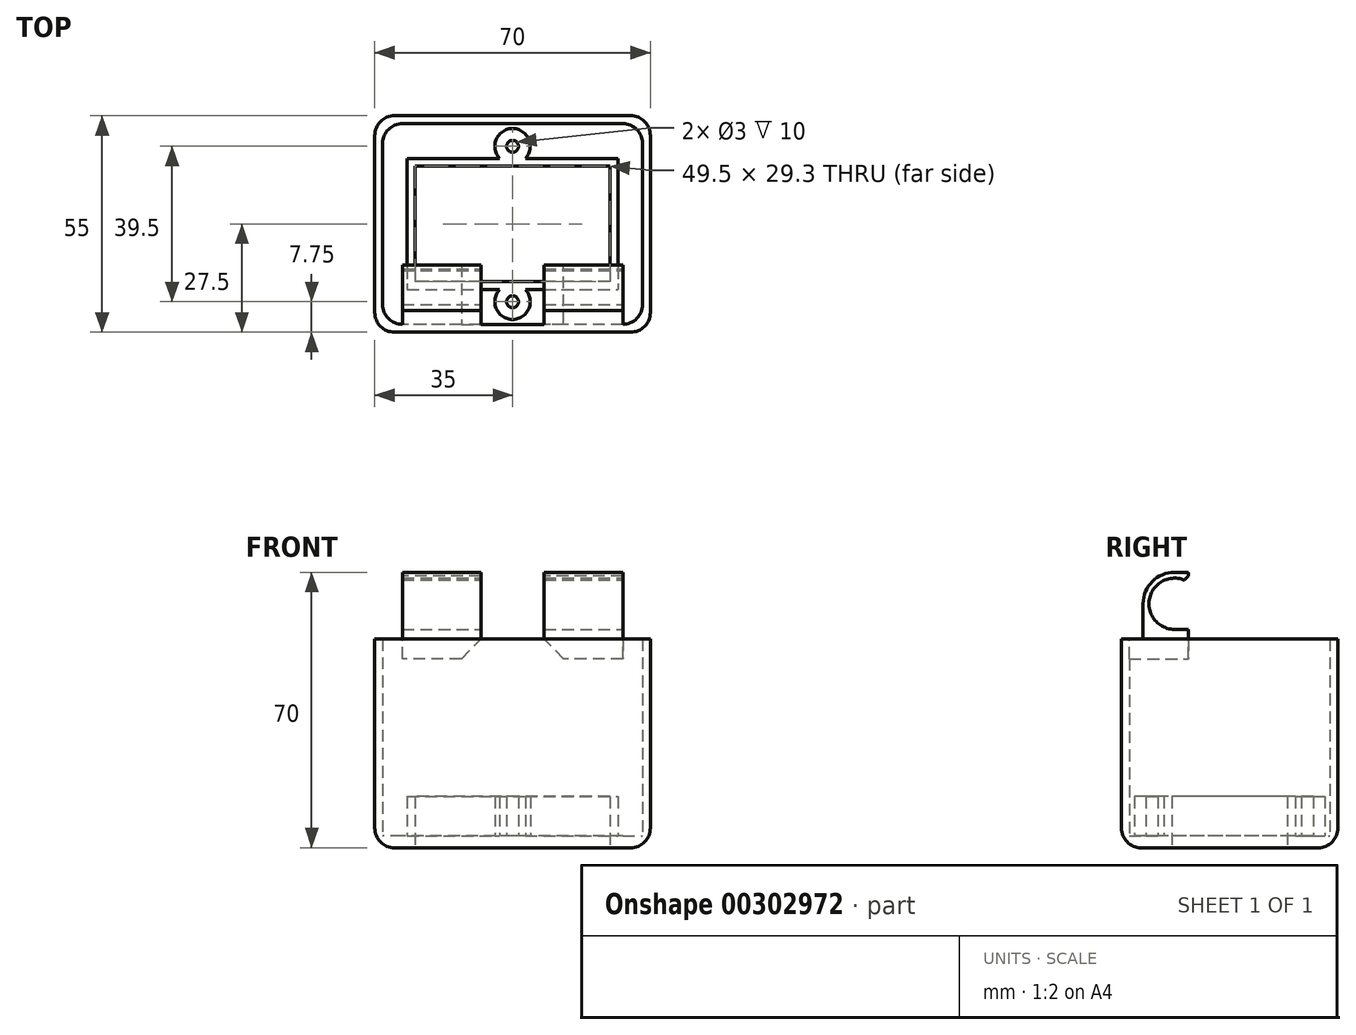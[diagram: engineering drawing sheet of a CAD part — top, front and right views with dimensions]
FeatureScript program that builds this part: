
annotation { "Feature Type Name" : "Feature", "Feature Type Description" : "" }
export const myFeature = defineFeature(function(context is Context, id is Id, definition is map)
    precondition{}
    {
        {
            var Q0;
            Q0=qCreatedBy(makeId("Top.planeOp"),FACE);
            var sketch = newSketch(context, id + "F0", { "sketchPlane" : qUnion([Q0])});
            skLineSegment(sketch, "E0.bottom", {"start": v(35, 27.5) * mm, "end": v(-35, 27.5) * mm});
            skLineSegment(sketch, "E0.top", {"start": v(35, -27.5) * mm, "end": v(-35, -27.5) * mm});
            skLineSegment(sketch, "E0.left", {"start": v(35, 27.5) * mm, "end": v(35, -27.5) * mm});
            skLineSegment(sketch, "E0.right", {"start": v(-35, 27.5) * mm, "end": v(-35, -27.5) * mm});
            skPoint(sketch, "E0.middle", {"position": v(0, 0) * mm});
            skLineSegment(sketch, "E1.bottom", {"start": v(24.75, 14.65) * mm, "end": v(-24.75, 14.65) * mm});
            skLineSegment(sketch, "E1.top", {"start": v(24.75, -14.65) * mm, "end": v(-24.75, -14.65) * mm});
            skLineSegment(sketch, "E1.left", {"start": v(24.75, 14.65) * mm, "end": v(24.75, -14.65) * mm});
            skLineSegment(sketch, "E1.right", {"start": v(-24.75, 14.65) * mm, "end": v(-24.75, -14.65) * mm});
            skSolve(sketch);
        }
        {
            var Q0;
            Q0=makeQuery(id+"F0.imprint","IMPRINT",FACE,{"disambiguationData":[TD([[makeQuery(id+"F0.imprint","IMPRINT",EDGE,{"derivedFrom":sQuery(id+"F0.wireOp",EDGE,"E0.bottom")}),1.0]])]});
            extrude(context, id + "F1", {"entities" : qUnion([Q0]), "depth" : 3 * mm, "offsetDistance" : 25 * mm});
        }
        {
            var Q0;
            Q0=makeQuery(id+"F1.opExtrude","CAP_FACE",FACE,{"disambiguationData":[OSD([sQuery(id+"F0.wireOp",EDGE,"E0.bottom"),sQuery(id+"F0.wireOp",EDGE,"E0.top"),sQuery(id+"F0.wireOp",EDGE,"E0.left"),sQuery(id+"F0.wireOp",EDGE,"E0.right"),sQuery(id+"F0.wireOp",EDGE,"E1.bottom"),sQuery(id+"F0.wireOp",EDGE,"E1.top"),sQuery(id+"F0.wireOp",EDGE,"E1.left"),sQuery(id+"F0.wireOp",EDGE,"E1.right")])],"isStart":false});
            var sketch = newSketch(context, id + "F2", { "sketchPlane" : qUnion([Q0])});
            skLineSegment(sketch, "E2.bottom", {"start": v(33, 25.5) * mm, "end": v(-33, 25.5) * mm});
            skLineSegment(sketch, "E2.top", {"start": v(33, -25.5) * mm, "end": v(-33, -25.5) * mm});
            skLineSegment(sketch, "E2.left", {"start": v(33, 25.5) * mm, "end": v(33, -25.5) * mm});
            skLineSegment(sketch, "E2.right", {"start": v(-33, 25.5) * mm, "end": v(-33, -25.5) * mm});
            skPoint(sketch, "E2.middle", {"position": v(0, 0) * mm});
            skLineSegment(sketch, "E3.bottom", {"start": v(-26.75, 16.65) * mm, "end": v(-3.26, 16.65) * mm});
            skLineSegment(sketch, "E3.top", {"start": v(-26.75, -16.65) * mm, "end": v(-3.26, -16.65) * mm});
            skLineSegment(sketch, "E3.left", {"start": v(-26.75, 16.65) * mm, "end": v(-26.75, -16.65) * mm});
            skLineSegment(sketch, "E3.right", {"start": v(26.75, 16.65) * mm, "end": v(26.75, -16.65) * mm});
            skLineSegment(sketch, "E4", {"start": v(0, 0) * mm, "end": v(0, 19.75) * mm, "construction": true});
            skLineSegment(sketch, "E5", {"start": v(0, 0) * mm, "end": v(0, -19.75) * mm, "construction": true});
            skPoint(sketch, "E5.endSnap0", {"position": v(0, -16.65) * mm});
            skCircle(sketch, "E6", {"center": v(0, 19.75) * mm, "radius": 1.5 * mm});
            skCircle(sketch, "E7", {"center": v(0, -19.75) * mm, "radius": 1.5 * mm});
            skArc(sketch, "E8", {"start": v(3.26, 16.65) * mm, "mid": v(0, 24.25) * mm, "end": v(-3.26, 16.65) * mm});
            skArc(sketch, "E9", {"start": v(-3.26, -16.65) * mm, "mid": v(0, -24.25) * mm, "end": v(3.26, -16.65) * mm});
            skLineSegment(sketch, "E10.trimOffspring", {"start": v(3.26, 16.65) * mm, "end": v(26.75, 16.65) * mm});
            skLineSegment(sketch, "E11.trimOffspring", {"start": v(3.26, -16.65) * mm, "end": v(26.75, -16.65) * mm});
            skSolve(sketch);
        }
        {
            var Q0;
            Q0=makeQuery(id+"F2.imprint","IMPRINT",FACE,{"disambiguationData":[TD([[makeQuery(id+"F2.imprint","IMPRINT",EDGE,{"derivedFrom":sQuery(id+"F2.wireOp",EDGE,"E3.bottom")}),-1.0]])]});
            extrude(context, id + "F3", {"entities" : qUnion([Q0]), "operationType" : NewBodyOperationType.ADD, "depth" : 10 * mm, "offsetDistance" : 25 * mm});
        }
        {
            var Q0;
            Q0=makeQuery(id+"F2.imprint","IMPRINT",FACE,{"disambiguationData":[TD([[makeQuery(id+"F2.imprint","IMPRINT",EDGE,{"derivedFrom":sQuery(id+"F2.wireOp",EDGE,"E2.bottom")}),-1.0]])]});
            extrude(context, id + "F4", {"entities" : qUnion([Q0]), "operationType" : NewBodyOperationType.ADD, "depth" : 50 * mm, "offsetDistance" : 25 * mm});
        }
        {
            var Q0;
            Q0=makeQuery(id+"F4.opExtrude","SWEPT_EDGE",EDGE,{"disambiguationData":[OSD([sQuery(id+"F2.wireOp",EDGE,"E2.bottom"),sQuery(id+"F2.wireOp",EDGE,"E2.right")])]});
            var Q1;
            Q1=makeQuery(id+"F4.opExtrude","SWEPT_EDGE",EDGE,{"disambiguationData":[OSD([sQuery(id+"F2.wireOp",EDGE,"E2.bottom"),sQuery(id+"F2.wireOp",EDGE,"E2.left")])]});
            var Q2;
            Q2=makeQuery(id+"F4.opExtrude","SWEPT_EDGE",EDGE,{"disambiguationData":[OSD([sQuery(id+"F2.wireOp",EDGE,"E2.top"),sQuery(id+"F2.wireOp",EDGE,"E2.right")])]});
            var Q3;
            Q3=makeQuery(id+"F4.opExtrude","SWEPT_EDGE",EDGE,{"disambiguationData":[OSD([sQuery(id+"F2.wireOp",EDGE,"E2.top"),sQuery(id+"F2.wireOp",EDGE,"E2.left")])]});
            var Q4;
            Q4=makeQuery(id+"F4.opExtrude","CAP_EDGE",EDGE,{"disambiguationData":[OSD([sQuery(id+"F2.wireOp",EDGE,"E2.bottom")])],"isStart":true});
            var Q5;
            Q5=makeQuery(id+"F4.opExtrude","CAP_EDGE",EDGE,{"disambiguationData":[OSD([sQuery(id+"F2.wireOp",EDGE,"E2.right")])],"isStart":true});
            var Q6;
            Q6=makeQuery(id+"F4.opExtrude","CAP_EDGE",EDGE,{"disambiguationData":[OSD([sQuery(id+"F2.wireOp",EDGE,"E2.left")])],"isStart":true});
            var Q7;
            Q7=makeQuery(id+"F4.opExtrude","CAP_EDGE",EDGE,{"disambiguationData":[OSD([sQuery(id+"F2.wireOp",EDGE,"E2.top")])],"isStart":true});
            var Q8;
            Q8=makeQuery(id+"F1.opExtrude","CAP_EDGE",EDGE,{"disambiguationData":[OSD([sQuery(id+"F0.wireOp",EDGE,"E0.right")])],"isStart":true});
            var Q9;
            {var subQ0=sQuery(id+"F0.wireOp",EDGE,"E0.right");var subQ1=sQuery(id+"F0.wireOp",EDGE,"E0.bottom");Q9=makeQuery(id+"F4.boolean.opBoolean","MERGE",EDGE,{"derivedFrom":[makeQuery(id+"F1.opExtrude","SWEPT_EDGE",EDGE,{"disambiguationData":[OSD([subQ1,subQ0])]}),makeQuery(id+"F4.opExtrude","SWEPT_EDGE",EDGE,{"disambiguationData":[OSD([subQ1,subQ0])]})]});}
            var Q10;
            {var subQ0=sQuery(id+"F0.wireOp",EDGE,"E0.right");var subQ1=sQuery(id+"F0.wireOp",EDGE,"E0.top");Q10=makeQuery(id+"F4.boolean.opBoolean","MERGE",EDGE,{"derivedFrom":[makeQuery(id+"F1.opExtrude","SWEPT_EDGE",EDGE,{"disambiguationData":[OSD([subQ1,subQ0])]}),makeQuery(id+"F4.opExtrude","SWEPT_EDGE",EDGE,{"disambiguationData":[OSD([subQ1,subQ0])]})]});}
            var Q11;
            Q11=makeQuery(id+"F1.opExtrude","CAP_EDGE",EDGE,{"disambiguationData":[OSD([sQuery(id+"F0.wireOp",EDGE,"E0.bottom")])],"isStart":true});
            var Q12;
            Q12=makeQuery(id+"F1.opExtrude","CAP_EDGE",EDGE,{"disambiguationData":[OSD([sQuery(id+"F0.wireOp",EDGE,"E0.top")])],"isStart":true});
            var Q13;
            Q13=makeQuery(id+"F1.opExtrude","CAP_EDGE",EDGE,{"disambiguationData":[OSD([sQuery(id+"F0.wireOp",EDGE,"E0.left")])],"isStart":true});
            var Q14;
            {var subQ0=sQuery(id+"F0.wireOp",EDGE,"E0.left");var subQ1=sQuery(id+"F0.wireOp",EDGE,"E0.bottom");Q14=makeQuery(id+"F4.boolean.opBoolean","MERGE",EDGE,{"derivedFrom":[makeQuery(id+"F1.opExtrude","SWEPT_EDGE",EDGE,{"disambiguationData":[OSD([subQ1,subQ0])]}),makeQuery(id+"F4.opExtrude","SWEPT_EDGE",EDGE,{"disambiguationData":[OSD([subQ1,subQ0])]})]});}
            var Q15;
            {var subQ0=sQuery(id+"F0.wireOp",EDGE,"E0.left");var subQ1=sQuery(id+"F0.wireOp",EDGE,"E0.top");Q15=makeQuery(id+"F4.boolean.opBoolean","MERGE",EDGE,{"derivedFrom":[makeQuery(id+"F1.opExtrude","SWEPT_EDGE",EDGE,{"disambiguationData":[OSD([subQ1,subQ0])]}),makeQuery(id+"F4.opExtrude","SWEPT_EDGE",EDGE,{"disambiguationData":[OSD([subQ1,subQ0])]})]});}
            fillet(context, id + "F5", {"entities" : qUnion([Q0, Q1, Q2, Q3, Q4, Q5, Q6, Q7, Q8, Q9, Q10, Q11, Q12, Q13, Q14, Q15]), "radius" : 5 * mm, "tangentPropagation" : true, "allowEdgeOverflow" : false});
        }
        {
            var Q0;
            Q0=makeQuery(id+"F4.opExtrude","CAP_FACE",FACE,{"disambiguationData":[OSD([sQuery(id+"F0.wireOp",EDGE,"E0.bottom"),sQuery(id+"F0.wireOp",EDGE,"E0.top"),sQuery(id+"F0.wireOp",EDGE,"E0.left"),sQuery(id+"F0.wireOp",EDGE,"E0.right"),sQuery(id+"F2.wireOp",EDGE,"E2.bottom"),sQuery(id+"F2.wireOp",EDGE,"E2.top"),sQuery(id+"F2.wireOp",EDGE,"E2.left"),sQuery(id+"F2.wireOp",EDGE,"E2.right")])],"isStart":false});
            var sketch = newSketch(context, id + "F6", { "sketchPlane" : qUnion([Q0])});
            skLineSegment(sketch, "E12.bottom", {"start": v(28, -25.5) * mm, "end": v(8, -25.5) * mm});
            skLineSegment(sketch, "E12.top", {"start": v(28, -10.5) * mm, "end": v(8, -10.5) * mm});
            skLineSegment(sketch, "E12.left", {"start": v(28, -25.5) * mm, "end": v(28, -10.5) * mm});
            skLineSegment(sketch, "E12.right", {"start": v(8, -25.5) * mm, "end": v(8, -10.5) * mm});
            skLineSegment(sketch, "E13.bottom", {"start": v(-28, -25.5) * mm, "end": v(-8, -25.5) * mm});
            skLineSegment(sketch, "E13.top", {"start": v(-28, -10.5) * mm, "end": v(-8, -10.5) * mm});
            skLineSegment(sketch, "E13.left", {"start": v(-28, -25.5) * mm, "end": v(-28, -10.5) * mm});
            skLineSegment(sketch, "E13.right", {"start": v(-8, -25.5) * mm, "end": v(-8, -10.5) * mm});
            skSolve(sketch);
        }
        {
            var Q0;
            Q0=makeQuery(id+"F6.imprint","IMPRINT",FACE,{"disambiguationData":[TD([[makeQuery(id+"F6.imprint","IMPRINT",EDGE,{"derivedFrom":sQuery(id+"F6.wireOp",EDGE,"E12.bottom")}),-1.0]])]});
            var Q1;
            Q1=makeQuery(id+"F6.imprint","IMPRINT",FACE,{"disambiguationData":[TD([[makeQuery(id+"F6.imprint","IMPRINT",EDGE,{"derivedFrom":sQuery(id+"F6.wireOp",EDGE,"E13.bottom")}),-1.0]])]});
            extrude(context, id + "F7", {"entities" : qUnion([Q0, Q1]), "operationType" : NewBodyOperationType.ADD, "oppositeDirection" : true, "depth" : 2 * mm, "offsetDistance" : 25 * mm});
        }
        {
            var Q0;
            Q0=makeQuery(id+"F7.opExtrude","SWEPT_FACE",FACE,{"disambiguationData":[OSD([sQuery(id+"F6.wireOp",EDGE,"E12.left")])]});
            var sketch = newSketch(context, id + "F8", { "sketchPlane" : qUnion([Q0])});
            skLineSegment(sketch, "E14", {"start": v(-25.5, 53) * mm, "end": v(-25.5, 62) * mm, "construction": true});
            skLineSegment(sketch, "E15", {"start": v(-25.5, 62) * mm, "end": v(-14, 62) * mm, "construction": true});
            skArc(sketch, "E16", {"start": v(-11.78, 68.1) * mm, "mid": v(-20.4, 63.13) * mm, "end": v(-14, 55.5) * mm});
            skArc(sketch, "E17", {"start": v(-14, 70) * mm, "mid": v(-19.66, 67.66) * mm, "end": v(-22, 62) * mm});
            skLineSegment(sketch, "E18", {"start": v(-22, 62) * mm, "end": v(-22, 53) * mm});
            skLineSegment(sketch, "E19", {"start": v(-14, 62) * mm, "end": v(-14, 70) * mm, "construction": true});
            skLineSegment(sketch, "E20", {"start": v(-10.5, 53) * mm, "end": v(-10.5, 55.5) * mm});
            skLineSegment(sketch, "E21", {"start": v(-10.5, 55.5) * mm, "end": v(-14, 55.5) * mm});
            skLineSegment(sketch, "E22", {"start": v(-14, 70) * mm, "end": v(-10.5, 70) * mm});
            skLineSegment(sketch, "E23", {"start": v(-10.5, 70) * mm, "end": v(-10.5, 68.1) * mm});
            skLineSegment(sketch, "E24", {"start": v(-10.5, 68.1) * mm, "end": v(-11.78, 68.1) * mm});
            skSolve(sketch);
        }
        {
            var Q0;
            {var subQ1=sQuery(id+"F8.wireOp",EDGE,"E16");Q0=makeQuery(id+"F8.imprint","IMPRINT",FACE,{"disambiguationData":[TD([[makeQuery(id+"F8.imprint","IMPRINT",EDGE,{"derivedFrom":subQ1}),-1.0]])]});}
            extrude(context, id + "F9", {"entities" : qUnion([Q0]), "operationType" : NewBodyOperationType.ADD, "oppositeDirection" : true, "depth" : 56 * mm, "offsetDistance" : 25 * mm});
        }
        {
            var Q0;
            Q0=makeQuery(id+"F9.opExtrude","SWEPT_FACE",FACE,{"disambiguationData":[OSD([sQuery(id+"F8.wireOp",EDGE,"E18")])]});
            var sketch = newSketch(context, id + "F10", { "sketchPlane" : qUnion([Q0])});
            skLineSegment(sketch, "E25.bottom", {"start": v(8, 53) * mm, "end": v(-8, 53) * mm});
            skLineSegment(sketch, "E25.top", {"start": v(8, 75.24) * mm, "end": v(-8, 75.24) * mm});
            skLineSegment(sketch, "E25.left", {"start": v(8, 53) * mm, "end": v(8, 75.24) * mm});
            skLineSegment(sketch, "E25.right", {"start": v(-8, 53) * mm, "end": v(-8, 75.24) * mm});
            skSolve(sketch);
        }
        {
            var Q0;
            {var subQ0=sQuery(id+"F10.wireOp",EDGE,"E25.bottom");Q0=makeQuery(id+"F10.imprint","IMPRINT",FACE,{"disambiguationData":[TD([[makeQuery(id+"F10.imprint","IMPRINT",EDGE,{"derivedFrom":subQ0}),1.0]])]});}
            var Q1;
            {var subQ0=sQuery(id+"F10.wireOp",EDGE,"E25.top");Q1=makeQuery(id+"F10.imprint","IMPRINT",FACE,{"disambiguationData":[TD([[makeQuery(id+"F10.imprint","IMPRINT",EDGE,{"derivedFrom":subQ0}),1.0]])]});}
            extrude(context, id + "F11", {"entities" : qUnion([Q0, Q1]), "operationType" : NewBodyOperationType.REMOVE, "oppositeDirection" : true, "depth" : 25 * mm, "offsetDistance" : 25 * mm});
        }
        {
            var Q0;
            Q0=makeQuery(id+"F7.opExtrude","CAP_FACE",FACE,{"disambiguationData":[OSD([sQuery(id+"F6.wireOp",EDGE,"E12.bottom"),sQuery(id+"F6.wireOp",EDGE,"E12.top"),sQuery(id+"F6.wireOp",EDGE,"E12.left"),sQuery(id+"F6.wireOp",EDGE,"E12.right")])],"isStart":false});
            var Q1;
            Q1=makeQuery(id+"F7.opExtrude","CAP_FACE",FACE,{"disambiguationData":[OSD([sQuery(id+"F6.wireOp",EDGE,"E13.bottom"),sQuery(id+"F6.wireOp",EDGE,"E13.top"),sQuery(id+"F6.wireOp",EDGE,"E13.left"),sQuery(id+"F6.wireOp",EDGE,"E13.right")])],"isStart":false});
            extrude(context, id + "F12", {"entities" : qUnion([Q0, Q1]), "operationType" : NewBodyOperationType.ADD, "depth" : 3 * mm, "offsetDistance" : 25 * mm});
        }
        {
            var Q0;
            Q0=makeQuery(id+"F12.opExtrude","CAP_EDGE",EDGE,{"disambiguationData":[OSD([sQuery(id+"F6.wireOp",EDGE,"E13.right")])],"isStart":false});
            var Q1;
            Q1=makeQuery(id+"F12.opExtrude","CAP_EDGE",EDGE,{"disambiguationData":[OSD([sQuery(id+"F6.wireOp",EDGE,"E12.right")])],"isStart":false});
            chamfer(context, id + "F13", {"entities" : qUnion([Q0, Q1]), "width" : 5 * mm, "tangentPropagation" : true});
        }
        {
            var Q0;
            {var subQ0=sQuery(id+"F8.wireOp",EDGE,"E23");var subQ1=sQuery(id+"F8.wireOp",EDGE,"E24");var subQ2=sQuery(id+"F6.wireOp",EDGE,"E12.left");Q0=makeQuery(id+"F11.boolean.opBoolean","SPLIT",EDGE,{"disambiguationData":[TD([makeQuery(id+"F7.opExtrude","SWEPT_FACE",FACE,{"disambiguationData":[OSD([subQ2])]})])],"derivedFrom":makeQuery(id+"F9.opExtrude","SWEPT_EDGE",EDGE,{"disambiguationData":[OSD([subQ0,subQ1])]})});}
            var Q1;
            {var subQ0=sQuery(id+"F8.wireOp",EDGE,"E23");var subQ1=sQuery(id+"F8.wireOp",EDGE,"E24");Q1=makeQuery(id+"F11.boolean.opBoolean","SPLIT",EDGE,{"disambiguationData":[TD([makeQuery(id+"F7.opExtrude","SWEPT_FACE",FACE,{"disambiguationData":[OSD([sQuery(id+"F6.wireOp",EDGE,"E13.left")])]})])],"derivedFrom":makeQuery(id+"F9.opExtrude","SWEPT_EDGE",EDGE,{"disambiguationData":[OSD([subQ0,subQ1])]})});}
            chamfer(context, id + "F14", {"entities" : qUnion([Q0, Q1]), "width" : 1 * mm, "tangentPropagation" : true});
        }
    });
